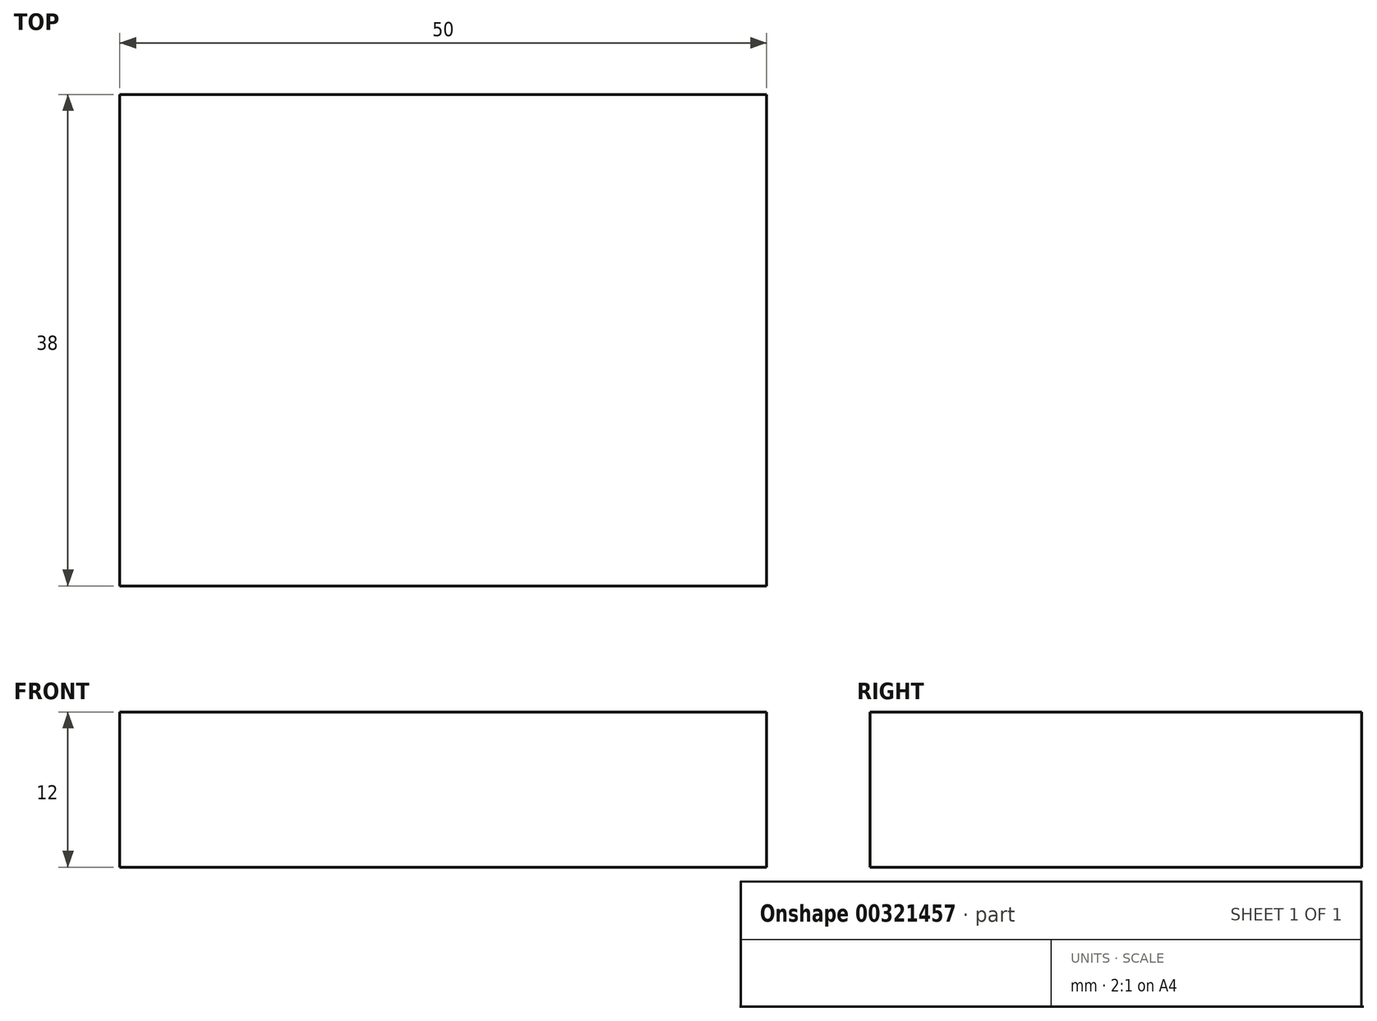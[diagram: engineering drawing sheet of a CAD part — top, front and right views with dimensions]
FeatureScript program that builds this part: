
annotation { "Feature Type Name" : "Feature", "Feature Type Description" : "" }
export const myFeature = defineFeature(function(context is Context, id is Id, definition is map)
    precondition{}
    {
        {
            var Q0;
            Q0=qCreatedBy(makeId("Top.planeOp"),FACE);
            var sketch = newSketch(context, id + "F0", { "sketchPlane" : qUnion([Q0])});
            skLineSegment(sketch, "E0.bottom", {"start": v(-25, 19) * mm, "end": v(25, 19) * mm});
            skLineSegment(sketch, "E0.top", {"start": v(-25, -19) * mm, "end": v(25, -19) * mm});
            skLineSegment(sketch, "E0.left", {"start": v(-25, 19) * mm, "end": v(-25, -19) * mm});
            skLineSegment(sketch, "E0.right", {"start": v(25, 19) * mm, "end": v(25, -19) * mm});
            skPoint(sketch, "E0.middle", {"position": v(0, 0) * mm});
            skSolve(sketch);
        }
        {
            var Q0;
            Q0 = qSketchRegion(id + "F0", true);
            extrude(context, id + "F1", {"entities" : qUnion([Q0]), "depth" : 12 * mm, "offsetDistance" : 25 * mm});
        }
    });
